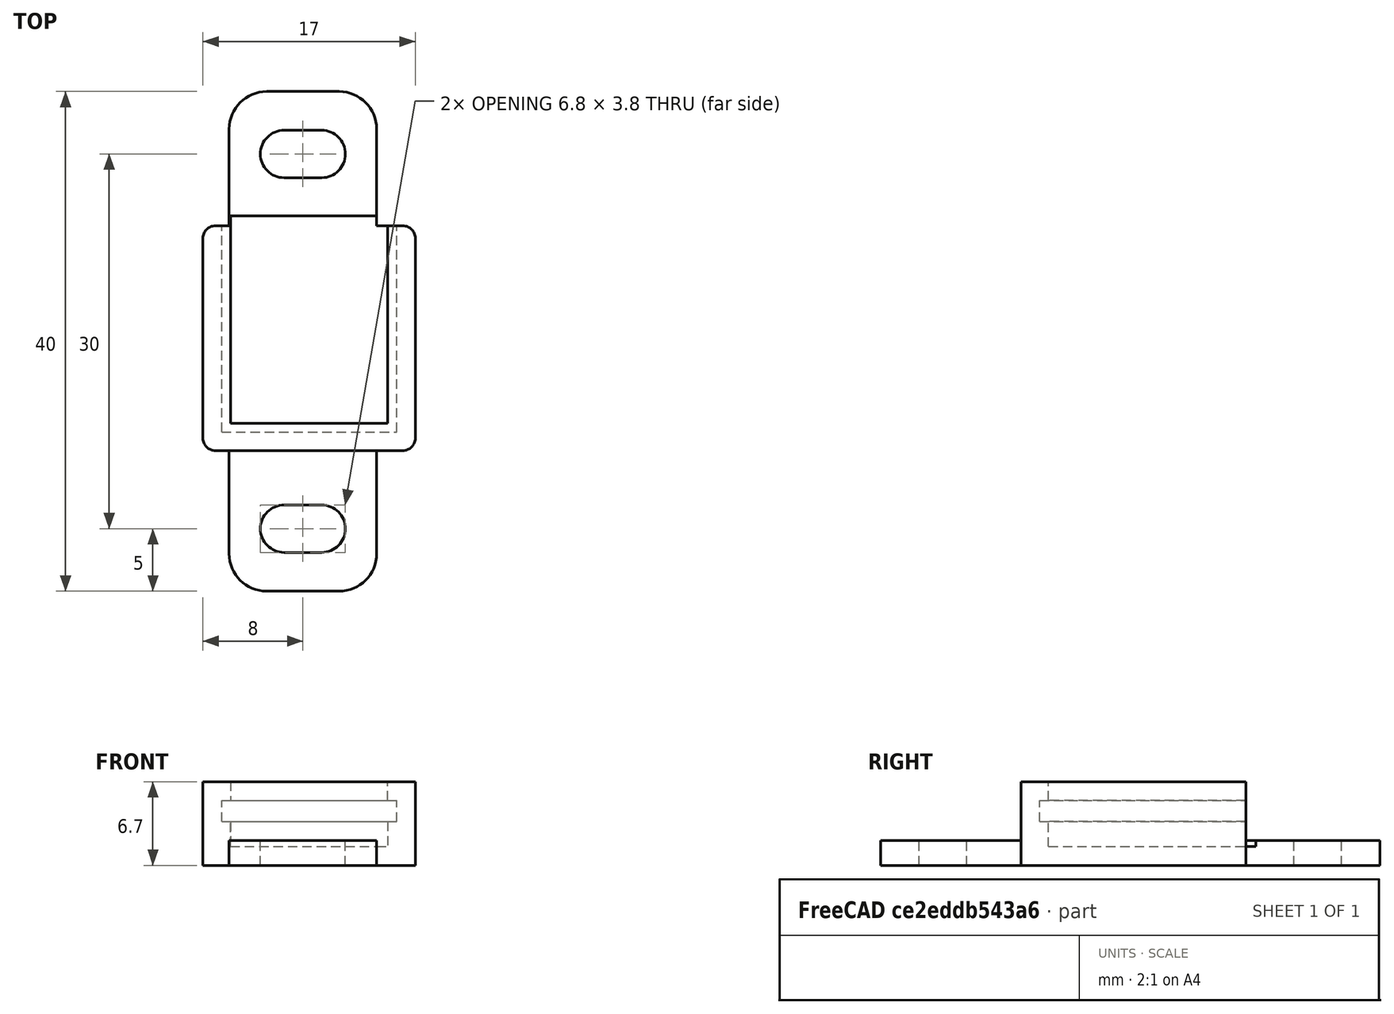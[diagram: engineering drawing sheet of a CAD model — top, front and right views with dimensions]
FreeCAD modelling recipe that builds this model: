
FCSTD DOCUMENT  (FreeCAD 0.19R)
Label: level_shifter_blue6pins
License: FreeArt
LicenseURL: http://artlibre.org/licence/lal
objects: Part::Box×3, Part::MultiFuse×2, Spreadsheet::Sheet×1, Part::Fillet×1, Part::Feature×1, Part::Cut×1, App::Part×1
note: 8 computed .brp shape members not serialized (recipe doc carries the construction recipe); baked Part::Feature solids carry a one-line shape summary decoded from their .brp

FEATURE [Spreadsheet::Sheet] Spreadsheet  label="p"
  cells = A1=pcb_x; B1(pcb_x)=14; A2=pcb_y; B2(pcb_y)=16.5; A3=pcb_z; B3(pcb_z)=1.7; A4=pcb_under; B4(pcb_under)=2; A5=side_wall; B5(side_wall)=1.5; A6=pcb_side_lane; B6(pcb_side_lane)=0.7; A7=bottom_wall; B7(bottom_wall)=1.5; A8=pcb_above; B8(pcb_above)=1.5
FEATURE [Part::Box] Box  label="external cube"
  AttacherType = Attacher::AttachEngine3D
  Height = 6.7
  Length = 17
  Width = 18
  expr: Height = <<p>>.bottom_wall + <<p>>.pcb_under + <<p>>.pcb_z + <<p>>.pcb_above
  expr: Width = <<p>>.pcb_y + <<p>>.side_wall
  expr: Length = <<p>>.pcb_x + 2 * <<p>>.side_wall
FEATURE [Part::Box] Box006  label="internal cube"
  AttacherType = Attacher::AttachEngine3D
  Height = 5.2
  Length = 12.6
  Placement = pos=(2.2,2.2,1.5) rot=(0,0,1;0rad)
  Width = 16.6
  expr: .Placement.Base.y = <<p>>.side_wall + <<p>>.pcb_side_lane
  expr: .Placement.Base.x = <<p>>.side_wall + <<p>>.pcb_side_lane
  expr: .Placement.Base.z = <<p>>.bottom_wall
  expr: Height = <<p>>.pcb_under + <<p>>.pcb_z + <<p>>.pcb_above
  expr: Width = <<p>>.pcb_y - 2 * <<p>>.pcb_side_lane + <<p>>.side_wall
  expr: Length = <<p>>.pcb_x - 2 * <<p>>.pcb_side_lane
FEATURE [Part::Box] Box007  label="pcb extract cube"
  AttacherType = Attacher::AttachEngine3D
  Height = 1.7
  Length = 14
  Placement = pos=(1.5,1.5,3.5) rot=(0,0,1;0rad)
  Width = 16.5
  expr: .Placement.Base.y = <<p>>.side_wall
  expr: .Placement.Base.x = <<p>>.side_wall
  expr: Length = <<p>>.pcb_x
  expr: Width = <<p>>.pcb_y
  expr: .Placement.Base.z = <<p>>.bottom_wall + <<p>>.pcb_under
  expr: Height = <<p>>.pcb_z
FEATURE [Part::MultiFuse] Fusion  label="extract fusion"
  Shapes = -> [Box006,Box007]
FEATURE [Part::Fillet] Fillet  label="external fillet"
  Base = -> Box
  Edges = 4 edges r=1: [Edge1,Edge3,Edge5,Edge7]
FEATURE [Part::Feature] Cut002001  label="attach plane y dir001"
  Placement = pos=(2.1,-11.25,0) rot=(0,0,1;0rad)
  shape: bbox 11.8 x 40 x 2 mm, 20 faces (baked)
FEATURE [Part::MultiFuse] Fusion001  label="body fusion"
  Shapes = -> [Fillet,Cut002001]
FEATURE [Part::Cut] Cut  label="body cut"
  Base = -> Fusion001
  Tool = -> Fusion
FEATURE [App::Part] Part  label="buzzer pcb box part"
  Group = -> [Box,Fillet,Fusion001,Fusion,Box007,Box006,Cut]
  Origin = -> Origin
